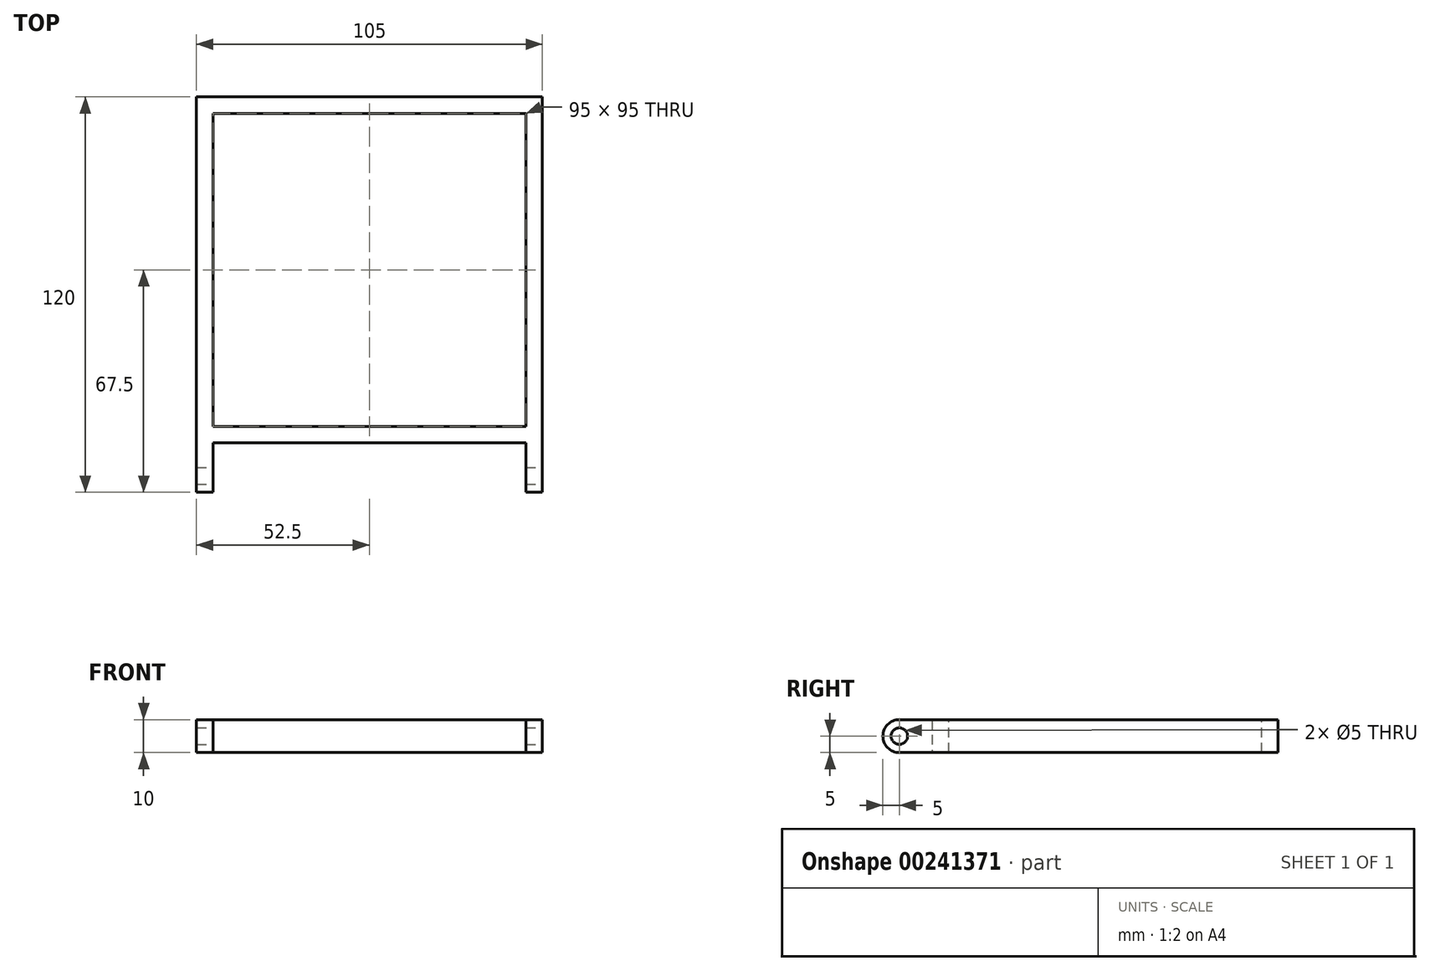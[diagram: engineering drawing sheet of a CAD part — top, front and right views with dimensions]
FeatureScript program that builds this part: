
annotation { "Feature Type Name" : "Feature", "Feature Type Description" : "" }
export const myFeature = defineFeature(function(context is Context, id is Id, definition is map)
    precondition{}
    {
        {
            var Q0;
            Q0=qCreatedBy(makeId("Top.planeOp"),FACE);
            var sketch = newSketch(context, id + "F0", { "sketchPlane" : qUnion([Q0])});
            skLineSegment(sketch, "E0.bottom", {"start": v(-52.5, 52.5) * mm, "end": v(52.5, 52.5) * mm});
            skLineSegment(sketch, "E0.top", {"start": v(-52.5, -52.5) * mm, "end": v(52.5, -52.5) * mm});
            skLineSegment(sketch, "E0.left", {"start": v(-52.5, 52.5) * mm, "end": v(-52.5, -52.5) * mm});
            skLineSegment(sketch, "E0.right", {"start": v(52.5, 52.5) * mm, "end": v(52.5, -52.5) * mm});
            skPoint(sketch, "E0.middle", {"position": v(0, 0) * mm});
            skLineSegment(sketch, "E1.bottom", {"start": v(-52.5, -52.5) * mm, "end": v(-47.5, -52.5) * mm});
            skLineSegment(sketch, "E1.top", {"start": v(-52.5, -67.5) * mm, "end": v(-47.5, -67.5) * mm});
            skLineSegment(sketch, "E1.left", {"start": v(-52.5, -52.5) * mm, "end": v(-52.5, -67.5) * mm});
            skLineSegment(sketch, "E1.right", {"start": v(-47.5, -52.5) * mm, "end": v(-47.5, -67.5) * mm});
            skLineSegment(sketch, "E2.bottom", {"start": v(52.5, -52.5) * mm, "end": v(47.5, -52.5) * mm});
            skLineSegment(sketch, "E2.top", {"start": v(52.5, -67.5) * mm, "end": v(47.5, -67.5) * mm});
            skLineSegment(sketch, "E2.left", {"start": v(52.5, -52.5) * mm, "end": v(52.5, -67.5) * mm});
            skLineSegment(sketch, "E2.right", {"start": v(47.5, -52.5) * mm, "end": v(47.5, -67.5) * mm});
            skSolve(sketch);
        }
        {
            var Q0;
            Q0 = qSketchRegion(id + "F0", true);
            extrude(context, id + "F1", {"entities" : qUnion([Q0]), "depth" : 10 * mm});
        }
        {
            var Q0;
            Q0=makeQuery(id+"F1.opExtrude","SWEPT_FACE",FACE,{"disambiguationData":[OSD([sQuery(id+"F0.wireOp",EDGE,"E0.right"),sQuery(id+"F0.wireOp",EDGE,"E2.left")])]});
            var sketch = newSketch(context, id + "F2", { "sketchPlane" : qUnion([Q0])});
            skCircle(sketch, "E3", {"center": v(-62.5, 5) * mm, "radius": 2.5 * mm});
            skPoint(sketch, "E3.centerSnap0", {"position": v(-67.5, 5) * mm});
            skSolve(sketch);
        }
        {
            var Q0;
            Q0 = qSketchRegion(id + "F2", true);
            extrude(context, id + "F3", {"entities" : qUnion([Q0]), "operationType" : NewBodyOperationType.REMOVE, "endBound" : BoundingType.THROUGH_ALL, "oppositeDirection" : true, "depth" : 25 * mm});
        }
        {
            var Q0;
            Q0=makeQuery(id+"F1.opExtrude","CAP_EDGE",EDGE,{"disambiguationData":[OSD([sQuery(id+"F0.wireOp",EDGE,"E1.top")])],"isStart":false});
            var Q1;
            Q1=makeQuery(id+"F1.opExtrude","CAP_EDGE",EDGE,{"disambiguationData":[OSD([sQuery(id+"F0.wireOp",EDGE,"E1.top")])],"isStart":true});
            var Q2;
            Q2=makeQuery(id+"F1.opExtrude","CAP_EDGE",EDGE,{"disambiguationData":[OSD([sQuery(id+"F0.wireOp",EDGE,"E2.top")])],"isStart":false});
            var Q3;
            Q3=makeQuery(id+"F1.opExtrude","CAP_EDGE",EDGE,{"disambiguationData":[OSD([sQuery(id+"F0.wireOp",EDGE,"E2.top")])],"isStart":true});
            fillet(context, id + "F4", {"entities" : qUnion([Q0, Q1, Q2, Q3]), "radius" : 5 * mm, "tangentPropagation" : true, "allowEdgeOverflow" : false});
        }
        {
            var Q0;
            Q0=makeQuery(id+"F1.opExtrude","CAP_FACE",FACE,{"disambiguationData":[OSD([sQuery(id+"F0.wireOp",EDGE,"E0.bottom"),sQuery(id+"F0.wireOp",EDGE,"E0.top"),sQuery(id+"F0.wireOp",EDGE,"E0.left"),sQuery(id+"F0.wireOp",EDGE,"E0.right"),sQuery(id+"F0.wireOp",EDGE,"E1.top"),sQuery(id+"F0.wireOp",EDGE,"E1.left"),sQuery(id+"F0.wireOp",EDGE,"E1.right"),sQuery(id+"F0.wireOp",EDGE,"E2.top"),sQuery(id+"F0.wireOp",EDGE,"E2.left"),sQuery(id+"F0.wireOp",EDGE,"E2.right")])],"isStart":false});
            var sketch = newSketch(context, id + "F5", { "sketchPlane" : qUnion([Q0])});
            skLineSegment(sketch, "E4.bottom", {"start": v(47.5, -47.5) * mm, "end": v(-47.5, -47.5) * mm});
            skLineSegment(sketch, "E4.top", {"start": v(47.5, 47.5) * mm, "end": v(-47.5, 47.5) * mm});
            skLineSegment(sketch, "E4.left", {"start": v(47.5, -47.5) * mm, "end": v(47.5, 47.5) * mm});
            skLineSegment(sketch, "E4.right", {"start": v(-47.5, -47.5) * mm, "end": v(-47.5, 47.5) * mm});
            skSolve(sketch);
        }
        {
            var Q0;
            Q0 = qSketchRegion(id + "F5", true);
            extrude(context, id + "F6", {"entities" : qUnion([Q0]), "operationType" : NewBodyOperationType.REMOVE, "endBound" : BoundingType.THROUGH_ALL, "oppositeDirection" : true, "depth" : 25 * mm});
        }
    });
